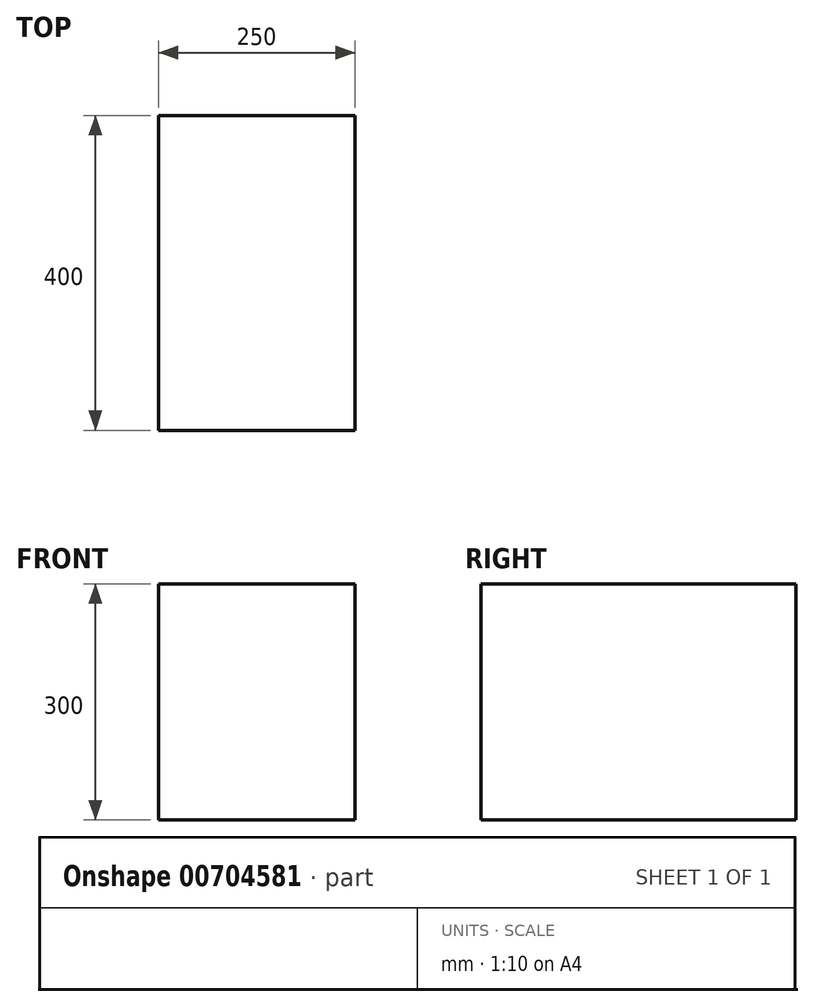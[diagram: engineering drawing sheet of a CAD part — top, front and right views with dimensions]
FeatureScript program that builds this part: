
annotation { "Feature Type Name" : "Feature", "Feature Type Description" : "" }
export const myFeature = defineFeature(function(context is Context, id is Id, definition is map)
    precondition{}
    {
        {
            var Q0;
            Q0=qCreatedBy(makeId("Top.planeOp"),FACE);
            var sketch = newSketch(context, id + "F0", { "sketchPlane" : qUnion([Q0])});
            skLineSegment(sketch, "E0.bottom", {"start": v(0, 200) * mm, "end": v(250, 200) * mm});
            skLineSegment(sketch, "E0.top", {"start": v(0, -200) * mm, "end": v(250, -200) * mm});
            skLineSegment(sketch, "E0.left", {"start": v(0, 200) * mm, "end": v(0, -200) * mm});
            skLineSegment(sketch, "E0.right", {"start": v(250, 200) * mm, "end": v(250, -200) * mm});
            skSolve(sketch);
        }
        {
            var Q0;
            Q0 = qSketchRegion(id + "F0", true);
            extrude(context, id + "F1", {"entities" : qUnion([Q0]), "endBound" : BoundingType.SYMMETRIC, "depth" : 300 * mm, "offsetDistance" : 25 * mm});
        }
    });
